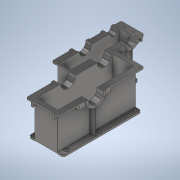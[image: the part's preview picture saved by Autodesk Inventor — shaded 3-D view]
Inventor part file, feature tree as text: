
AUTODESK INVENTOR PART (.ipt)
format: ipt  version: 2020 (Build 240168000, 168)  size: 1,747,456 bytes
history: native  units: mm
features: sketch x82, extrude x68, projected_geometry x43, fillet x26, plane x17, mirror x11, hole x10, other x7, reference x1
ambient origin geometry x8: Origin, YZ Plane, XZ Plane, XY Plane, X Axis, Y Axis, Z Axis, Center Point
bodies: 实体4 (feature_tree)
feature tree (265):
  sketch  "草图1"  dims[d0=41.0mm d1=40.0mm d2=41.0mm d3=8.0mm d4=41.0mm d5=41.0mm d6=40.0mm d7=8.0mm d8=25.0mm d9=71.0mm d10=8.0mm d11=70.0mm d12=190.0mm d13=75.0mm d14=43.0mm d15=8.0mm d16=75.0mm d17=40.0mm d18=31.0mm d19=12.0mm d20=25.0mm d21=10.0mm d22=8.0mm d23=30.0mm d24=5.0mm d25=25.0mm d26=174.0mm d27=91.0mm d28=40.0mm d29=21.0mm d30=71.0mm d31=12.0mm d32=30.0mm d33=30.0mm d34=25.0mm d35=12.0mm d36=30.0mm d37=30.0mm d38=100.0mm d39=40.0mm d40=12.0mm d41=20.0mm d42=70.0mm d43=15.0mm d44=2.0mm d45=31.0mm d56=8.0mm]
  plane  "工作平面6"
  extrude  "拉伸7"  Depth=8.0mm
  plane  "工作平面11"
  extrude  "拉伸35"  Depth=8.0mm
  extrude  "拉伸36"  [1 undecoded]
  extrude  "拉伸37"  Depth=30.0mm
  extrude  "拉伸38"  Depth=30.0mm
  extrude  "拉伸39"  Depth=30.0mm
  extrude  "拉伸40"  Depth=30.0mm
  extrude  "拉伸42"  Depth=10.0mm
  extrude  "拉伸43"  Depth=15.0mm TaperAngle=0.0deg
  plane  "工作平面12"
  mirror  "镜像2"
  extrude  "拉伸44"  Depth=15.0mm TaperAngle=0.0deg
  extrude  "拉伸45"  Depth=10.0mm TaperAngle=0.0deg
  extrude  "拉伸46"  Depth=15.0mm TaperAngle=0.0deg
  extrude  "拉伸47"  Depth=15.0mm TaperAngle=0.0deg
  extrude  "拉伸48"  Depth=15.0mm TaperAngle=0.0deg
  extrude  "拉伸49"  Depth=15.0mm TaperAngle=0.0deg
  extrude  "拉伸50"  Depth=15.0mm TaperAngle=0.0deg
  extrude  "拉伸51"  Depth=15.0mm TaperAngle=0.0deg
  extrude  "拉伸52"  Depth=15.0mm TaperAngle=0.0deg
  extrude  "拉伸53"  Depth=15.0mm TaperAngle=0.0deg
  extrude  "拉伸54"  Depth=25.0mm TaperAngle=0.0deg
  extrude  "拉伸55"  Depth=50.0mm
  extrude  "拉伸56"  Depth=50.0mm
  extrude  "拉伸57"  Depth=12.0mm
  extrude  "拉伸58"  Depth=70.0mm
  extrude  "拉伸59"  Depth=15.0mm TaperAngle=0.0deg
  extrude  "拉伸60"  Depth=68.869mm
  other  "对称面14"
  mirror  "镜像3"
  extrude  "拉伸62"  Depth=3.0mm TaperAngle=0.0deg
  mirror  "镜像4"
  fillet  "圆角1"  Radius=3.0mm
  fillet  "圆角2"  Radius=16.011mm
  extrude  "拉伸63"  Depth=16.153mm TaperAngle=0.0deg
  plane  "工作平面15"
  extrude  "拉伸64"  Depth=13.0mm TaperAngle=0.0deg
  extrude  "拉伸65"  Depth=60.0mm
  extrude  "拉伸66"  Depth=13.0mm TaperAngle=0.0deg
  plane  "工作平面16"
  mirror  "镜像5"
  mirror  "镜像6"
  extrude  "拉伸67"  Depth=13.0mm TaperAngle=0.0deg
  extrude  "拉伸68"  Depth=13.0mm TaperAngle=0.0deg
  extrude  "拉伸69"  Depth=13.0mm TaperAngle=0.0deg
  extrude  "拉伸70"  Depth=13.0mm TaperAngle=0.0deg
  extrude  "拉伸71"  Depth=13.0mm TaperAngle=0.0deg
  fillet  "圆角3"  Radius=13.0mm
  extrude  "拉伸72"  Depth=5.0mm
  fillet  "圆角4"  Radius=5.0mm
  extrude  "拉伸73"  Depth=5.0mm
  extrude  "拉伸74"  Depth=20.0mm
  extrude  "拉伸75"  Depth=28.0mm
  extrude  "拉伸76"  Depth=60.0mm
  extrude  "拉伸77"  Depth=28.0mm
  extrude  "拉伸78"  Depth=5.0mm TaperAngle=0.0deg
  extrude  "拉伸79"  Depth=10.0mm TaperAngle=0.0deg
  extrude  "拉伸80"  Depth=39.485mm
  extrude  "拉伸81"  Depth=18.0mm
  extrude  "拉伸82"  Depth=20.0mm TaperAngle=0.0deg
  extrude  "拉伸83"  Depth=40.0mm
  extrude  "拉伸84"  Depth=12.0mm
  extrude  "拉伸85"  Depth=30.0mm TaperAngle=0.0deg
  extrude  "拉伸86"  Depth=28.0mm
  extrude  "拉伸87"  Depth=16.0mm
  extrude  "拉伸88"  Depth=4.0mm TaperAngle=0.0deg
  extrude  "拉伸89"  Depth=25.307274mm
  fillet  "圆角5"  [1 undecoded]
  extrude  "拉伸90"  Depth=120.0mm
  extrude  "拉伸92"  Depth=4.0mm TaperAngle=0.0deg
  fillet  "圆角8"  Radius=30.0mm
  hole  "孔1"  [1 undecoded]
  extrude  "拉伸93"  Depth=1.0mm
  extrude  "拉伸94"  Depth=1.0mm
  sketch  "草图95"  dims[d363=13.835mm d364=36.0mm d365=28.0mm d366=2.0mm d367=90.0deg d368=41.3mm d369=0.0mm d370=25.307274mm d371=90.0deg]
  hole  "孔3"  [1 undecoded]
  hole  "孔4"  [1 undecoded]
  hole  "孔5"  [1 undecoded]
  plane  "工作平面18"
  plane  "工作平面19"
  extrude  "拉伸95"  Depth=105.0mm
  plane  "工作平面20"
  extrude  "拉伸96"  Depth=72.0mm
  mirror  "镜像7"
  extrude  "拉伸97"  Depth=40.0mm
  extrude  "拉伸98"  Depth=15.0mm
  hole  "孔6"  [1 undecoded]
  sketch  "草图107"  dims[d410=13.835mm d411=36.0mm d412=28.0mm d413=2.0mm d414=90.0deg d415=41.3mm d416=0.0mm d417=175.0mm]
  plane  "工作平面21"
  extrude  "拉伸99"  Depth=2.0mm
  extrude  "拉伸100"  Depth=2.0mm
  hole  "孔7"  [1 undecoded]
  plane  "工作平面22"
  plane  "工作平面23"
  plane  "工作平面24"
  other  "加强筋1"
  mirror  "镜像8"
  other  "加强筋2"
  other  "加强筋3"
  mirror  "镜像9"
  plane  "工作平面25"
  extrude  "拉伸101"  Depth=20.0mm
  hole  "孔8"  [1 undecoded]
  hole  "孔9"  [1 undecoded]
  plane  "工作平面26"
  mirror  "镜像10"
  hole  "孔10"  [1 undecoded]
  hole  "孔11"  [1 undecoded]
  plane  "工作平面27"
  mirror  "镜像11"
  extrude  "拉伸102"  Depth=2.0mm
  extrude  "拉伸103"  Depth=2.0mm
  plane  "工作平面28"
  mirror  "镜像12"
  fillet  "圆角9"  Radius=2.0mm
  fillet  "圆角10"  Radius=2.0mm
  fillet  "圆角11"  Radius=2.0mm
  fillet  "圆角12"  Radius=2.0mm
  fillet  "圆角13"  Radius=2.0mm
  fillet  "圆角14"  Radius=0.5mm
  fillet  "圆角15"  Radius=0.872665mm
  extrude  "拉伸104"  Depth=0.5mm
  fillet  "圆角16"  Radius=0.872665mm
  fillet  "圆角17"  Radius=0.5mm
  fillet  "圆角18"  Radius=0.872665mm
  fillet  "圆角19"  Radius=0.5mm
  fillet  "圆角20"  Radius=0.872665mm
  fillet  "圆角21"  Radius=0.5mm
  fillet  "圆角22"  Radius=0.872665mm
  fillet  "圆角23"  Radius=0.5mm
  fillet  "圆角24"  Radius=0.872665mm
  fillet  "圆角25"  Radius=0.5mm
  fillet  "圆角26"  Radius=0.872665mm
  fillet  "圆角27"  Radius=0.5mm
  fillet  "圆角28"  Radius=0.872665mm
  sketch  "草图9"  dims[d57=8.0mm d58=8.0mm]
  sketch  "草图36"  dims[d59=8.0mm d65=-360.0mm]
  sketch  "草图37"  dims[d66=30.0mm d67=30.0mm]
  sketch  "草图38"  dims[d68=30.0mm d69=30.0mm]
  sketch  "草图39"  dims[d70=30.0mm d71=30.0mm]
  sketch  "草图41"  dims[d72=30.0mm d73=30.0mm]
  sketch  "草图42"  dims[d74=15.0mm d75=0.0mm d139=10.0mm]
  sketch  "草图43"  dims[d140=10.0mm d141=15.0mm d142=0.0mm]
  sketch  "草图44"  dims[d143=15.0mm d144=0.0mm d145=15.0mm d146=0.0mm]
  sketch  "草图45"  dims[d147=10.0mm d148=0.0mm d149=10.0mm d150=0.0mm]
  sketch  "草图46"  dims[d151=10.0mm d152=0.0mm d155=15.0mm d156=0.0mm]
  sketch  "草图47"  dims[d157=15.0mm d158=0.0mm d159=15.0mm d160=0.0mm]
  sketch  "草图48"  dims[d161=15.0mm d162=0.0mm d163=15.0mm d164=0.0mm]
  projected_geometry  "投影回路6"
  sketch  "草图49"  dims[d165=15.0mm d166=0.0mm d167=15.0mm d168=0.0mm]
  sketch  "草图50"  dims[d169=15.0mm d170=0.0mm d171=15.0mm d172=0.0mm]
  sketch  "草图51"  dims[d173=15.0mm d174=0.0mm d175=15.0mm d176=0.0mm]
  sketch  "草图52"  dims[d177=15.0mm d178=0.0mm d179=15.0mm d180=0.0mm]
  sketch  "草图53"  dims[d181=15.0mm d182=0.0mm d183=15.0mm d184=0.0mm]
  sketch  "草图54"  dims[d185=5.0mm d186=0.0mm d187=25.0mm d188=0.0mm]
  sketch  "草图55"  dims[d189=25.807mm d190=0.0mm d191=50.0mm]
  projected_geometry  "投影回路7"
  sketch  "草图56"  dims[d192=46.0mm d193=0.0mm d194=50.0mm]
  projected_geometry  "投影回路8"
  projected_geometry  "投影回路9"
  sketch  "草图57"  dims[d198=50.0mm d199=0.0mm d200=12.0mm]
  projected_geometry  "投影回路10"
  sketch  "草图58"  dims[d201=12.0mm d202=70.0mm]
  projected_geometry  "投影回路11"
  sketch  "草图60"  dims[d203=46.0mm d204=0.0mm d205=15.0mm d206=0.0mm]
  sketch  "草图61"  dims[d207=23.0mm d208=0.0mm d209=68.869mm]
  projected_geometry  "投影回路12"
  sketch  "草图62"  dims[d210=46.0mm d211=0.0mm d212=3.0mm d213=0.0mm d214=3.0mm d215=0.0mm d216=16.011mm d217=0.0mm]
  sketch  "草图63"  dims[d218=3.0mm d219=0.0mm d220=16.153mm d221=0.0mm]
  projected_geometry  "投影回路13"
  sketch  "草图64"  dims[d222=20.0mm d223=13.0mm d224=0.0mm]
  projected_geometry  "投影回路14"
  sketch  "草图65"  dims[d225=12.0mm d226=60.0mm]
  plane  "工作平面17"
  sketch  "草图66"  dims[d227=13.0mm d228=0.0mm d229=13.0mm d230=0.0mm]
  projected_geometry  "投影回路15"
  sketch  "草图67"  dims[d231=13.0mm d232=0.0mm d233=13.0mm d234=0.0mm]
  projected_geometry  "投影回路16"
  sketch  "草图68"  dims[d235=13.0mm d236=0.0mm d237=13.0mm d238=0.0mm]
  projected_geometry  "投影回路17"
  sketch  "草图69"  dims[d239=13.0mm d240=0.0mm d241=13.0mm d242=0.0mm]
  projected_geometry  "投影回路18"
  sketch  "草图70"  dims[d243=13.0mm d244=0.0mm d245=13.0mm d246=0.0mm]
  projected_geometry  "投影回路19"
  sketch  "草图71"  dims[d247=13.0mm d248=0.0mm d249=13.0mm d250=0.0mm d251=13.0mm d252=0.0mm]
  projected_geometry  "投影回路20"
  sketch  "草图72"  dims[d253=5.0mm d254=0.0mm d255=5.0mm d256=5.0mm d257=0.0mm]
  sketch  "草图73"  dims[d258=5.0mm d259=0.0mm d260=5.0mm]
  projected_geometry  "投影回路21"
  sketch  "草图74"  dims[d261=5.0mm d262=0.0mm d263=20.0mm]
  projected_geometry  "投影回路22"
  sketch  "草图75"  dims[d265=5.0mm d266=0.0mm d267=28.0mm]
  projected_geometry  "投影回路23"
  sketch  "草图76"  dims[d269=35.0mm d270=60.0mm]
  projected_geometry  "投影回路24"
  sketch  "草图77"  dims[d271=28.0mm d274=28.0mm]
  projected_geometry  "投影回路25"
  sketch  "草图78"  dims[d275=60.0mm]
  projected_geometry  "投影回路26"
  sketch  "草图79"  dims[d276=20.0mm d277=6.0mm d278=45.0mm d279=2.0mm d280=90.0deg d281=8.0mm d282=20.594885mm d286=5.0mm d287=0.0mm]
  projected_geometry  "投影回路27"
  sketch  "草图80"  dims[d288=20.0mm d289=10.0mm d290=0.0mm]
  projected_geometry  "投影回路28"
  sketch  "草图81"  dims[d291=10.0mm d292=0.0mm]
  projected_geometry  "投影回路29"
  sketch  "草图82"  dims[d293=70.0mm d294=90.0mm d295=120.0mm d296=90.0mm d297=130.0mm d298=140.0mm d299=39.485mm]
  projected_geometry  "投影回路30"
  sketch  "草图83"  dims[d300=22.5mm]
  projected_geometry  "投影回路31"
  projected_geometry  "投影回路32"
  sketch  "草图84"  dims[d323=13.5mm d324=6.0mm d325=26.0mm d326=2.0mm d327=90.0deg d328=8.0mm d329=20.594885mm]
  projected_geometry  "投影回路33"
  sketch  "草图85"  dims[d330=13.5mm d331=6.0mm d332=26.0mm d333=2.0mm d334=90.0deg d335=8.0mm d336=20.594885mm d337=18.0mm]
  projected_geometry  "投影回路34"
  sketch  "草图86"  dims[d338=110.0mm]
  projected_geometry  "投影回路35"
  projected_geometry  "投影回路36"
  sketch  "草图87"  dims[d339=10.0mm d340=6.0mm d341=26.0mm d342=2.0mm d343=90.0deg d344=8.0mm d345=20.594885mm d346=20.0mm d347=0.0mm]
  sketch  "草图88"  dims[d348=-30.0mm d349=40.0mm]
  sketch  "草图89"  dims[d350=6.0mm d351=12.0mm]
  projected_geometry  "投影回路37"
  projected_geometry  "投影回路38"
  projected_geometry  "投影回路39"
  projected_geometry  "投影回路40"
  sketch  "草图90"  dims[d352=20.0mm d353=30.0mm d354=0.0mm]
  sketch  "草图92"  dims[d355=30.0mm d356=0.0mm d357=28.0mm]
  projected_geometry  "投影回路42"
  sketch  "草图93"  dims[d358=5.0mm d359=16.0mm]
  sketch  "草图94"  dims[d360=38.0mm d361=4.0mm d362=0.0mm]
  projected_geometry  "投影回路43"
  projected_geometry  "投影回路44"
  sketch  "草图98"  dims[d372=35.0mm d373=120.0mm]
  sketch  "草图99"  dims[d374=4.0mm d375=0.0mm d376=4.0mm d377=0.0mm]
  sketch  "草图100"  dims[d378=13.835mm d379=32.0mm d380=20.0mm d381=2.0mm d382=90.0deg d383=41.3mm d384=0.0mm d386=30.0mm]
  sketch  "草图101"  dims[d387=30.0mm d388=30.0mm]
  projected_geometry  "投影回路45"
  sketch  "草图102"  dims[d389=30.0mm]
  projected_geometry  "投影回路46"
  sketch  "草图104"  dims[d390=1.0mm d391=9.0mm d392=0.0mm d393=0.0mm d394=1.0mm d395=1.0mm d396=1.0mm]
  sketch  "草图105"  dims[d397=9.0mm d398=0.0mm d399=0.0mm d400=1.0mm d401=1.0mm d402=1.0mm]
  sketch  "草图106"  dims[d403=9.0mm d404=0.0mm d405=0.0mm d406=1.0mm d407=1.0mm d408=4.0mm d409=0.0mm]
  sketch  "草图108"  dims[d418=60.0mm d420=360.0deg]
  sketch  "草图109"  dims[d422=8.376mm d423=15.0mm d424=4.0mm d425=2.0mm d426=90.0deg d427=18.0mm d428=20.594885mm d429=165.0mm]
  projected_geometry  "投影回路48"
  sketch  "草图110"  dims[d430=60.0mm d432=360.0deg]
  sketch  "草图111"  dims[d434=8.376mm d435=15.0mm d436=4.0mm d437=2.0mm d438=90.0deg d439=18.0mm d440=20.594885mm d441=105.0mm]
  sketch  "草图112"  dims[d442=60.0mm d444=360.0deg]
  sketch  "草图113"  dims[d446=8.376mm d447=15.0mm d448=4.0mm d449=2.0mm d450=90.0deg d451=18.0mm d452=20.594885mm d453=72.0mm]
  sketch  "草图114"  dims[d454=10.0mm d455=0.0mm d456=40.0mm]
  sketch  "草图115"  dims[d457=10.0mm d458=15.0mm]
  sketch  "草图116"  dims[d459=20.0mm d460=0.0mm d461=19.0mm]
  projected_geometry  "投影回路49"
  sketch  "草图117"  dims[d462=19.0mm d463=2.0mm]
  sketch  "草图118"  dims[d464=12.0mm d465=2.0mm]
  sketch  "草图119"  dims[d466=2.0mm d467=1.0mm]
  reference  "参考1"
  sketch  "草图120"  dims[d468=25.0mm d469=0.0mm d470=20.0mm]
  sketch  "草图121"  dims[d471=20.0mm d472=12.0mm d473=20.0mm d474=2.0mm d475=2.0mm d476=2.0mm d477=2.0mm d478=2.0mm d479=2.0mm d480=2.0mm d481=2.0mm d482=2.0mm d78=0.5mm d79=0.872665mm d80=0.5mm d81=0.872665mm d106=0.5mm d107=0.872665mm d108=0.5mm d109=0.872665mm d111=0.5mm d112=0.872665mm d113=0.5mm d114=0.872665mm d126=0.5mm d127=0.872665mm d128=0.5mm d129=0.872665mm]
  projected_geometry  "投影回路50"
  other  "<userpath>\Desktop\111111\Workspace\cpz assemble.iam"
  other  "cpz assemble.iam"
  other  "垫片1:2"
note: 12 required parameter values undecoded (feature->parameter linkage not recoverable at this tier; creation-order binding heuristic only, values carry confidence <= 0.55)
